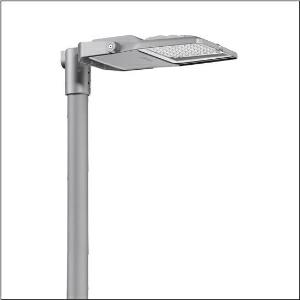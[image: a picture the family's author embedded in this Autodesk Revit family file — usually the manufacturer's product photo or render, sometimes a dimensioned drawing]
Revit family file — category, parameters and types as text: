
# Revit family: floodlight_fl_21_iq_mini___pl33t_5xa7772d2f3a_d038
name_source: partatom
category: Lighting Fixtures
units: mm (PartAtom-declared; Revit-internal decimal feet)

## family parameters
Cut with Voids When Loaded = No
Host = Face
Light Source = No
Part Type = Normal
Room Calculation Point = No
Round Connector Dimension = Use Diameter
Shared = No

## types (1)
- --- (1 x LED, 17620 lm, 143 W, 3000K)
    Apparent Load = 143 VA
    CIE Flux Codes = 26 75 99 100 100
    Color Rendering = 70
    Color Temperature = 3000K
    Default Elevation = 1800 mm
    Description = Floodlight FL 21 iQ mini, floodlight, primary light control with lens, of PMMA, primary optical cover: protective disc, of toughened safety glass, transparent, light distribution: PL33T, light emission: direct distribution, installation type: surface-mounted, LED, High Power LED, rated luminous flux: 17.620lm, luminous efficacy: 123lm/W, light colour: 730, colour temperature: 3000K, control: Auto-Match, Temp-Guard, Night-Set, Smart-Wire, Desk-Remote (wireless, voltage-free reading and setting of iQ features in the workshop via application-optimized NFC function/RFID function), optimised constant luminous flux control (CLO 2.0), Light-Fading, Lumen-Switch, with terminal, 6-pole, mains connection: 220..240V, AC, 50/60Hz, start of lifetime: 143W, end of service life: 152W, reduction: 61W, luminaire housing, of diecast aluminium, powder-coated, Siteco® metallic grey (DB 702S), corrosivity category C5 mid according to DIN EN ISO 12944, sealing non-destructively replaceable, please order mast flange separately, mast bracket, of steel, galvanised, powder-coated, protection rating (complete): IP66, insulation class (complete): insulation class II (safety insulation), certification: CE, ENEC, VDE, protection symbol: D, impact resistance: IK08, permissible operating ambient temperature: -40..+40°C, permissible operating ambient temperature for outdoor applications: -40..+50°C, standard: DIN EN 12944, LABS conformity tested according to VDMA 24364:2018-05, packaging unit: 1 piece

Light Distribution: PL33T
    Height = 70 mm
    Lamp = 1 x LED
    Lamp Light Flux = 17620 lm
    Lamp Power = 143 W
    Lamp count = 1
    Length = 485 mm
    Luminous efficacy = 123 lm/W
    Manufacturer = Siteco
    ModVariant = No
    Model = 5XA7772D2F3A
    Number of Poles = 1
    OnlyDefault = Yes
    Power Factor = 1
    Product Name = Floodlight FL 21 iQ mini | PL33T
    Product group = floodlight | pylon annexe
    ProductGroupID = 6200
    Protection Class = Protection class II
    Protection Degree = IP 66
    RLX_Detail_Level = 1
    RLX_Emergency_Light_Flux = 0 lm
    RLX_Emergency_Type = 0
    RLX_Emergency_Type_DB = No
    RlxData = <blob elided: 101409 chars, md5=edecb42e>
    Socket = socket
    Standby Power = 0 W
    System Light Flux = 17620 lm
    System Power = 143 W
    Type Comments = factory setting: luminous flux: 100 % | dim-lin: 254 | 730 mA
    Type Image = l_1007125.jpg
    URL = http://relux.com
    VarID = @adj_099089
    Voltage = 0 V
    Weight = 0.00 kg
    Width = 337 mm

## geometry (parser evidence)
native form markers: Blend x4, Sweep x12
no freeform markers — native parametric forms only
